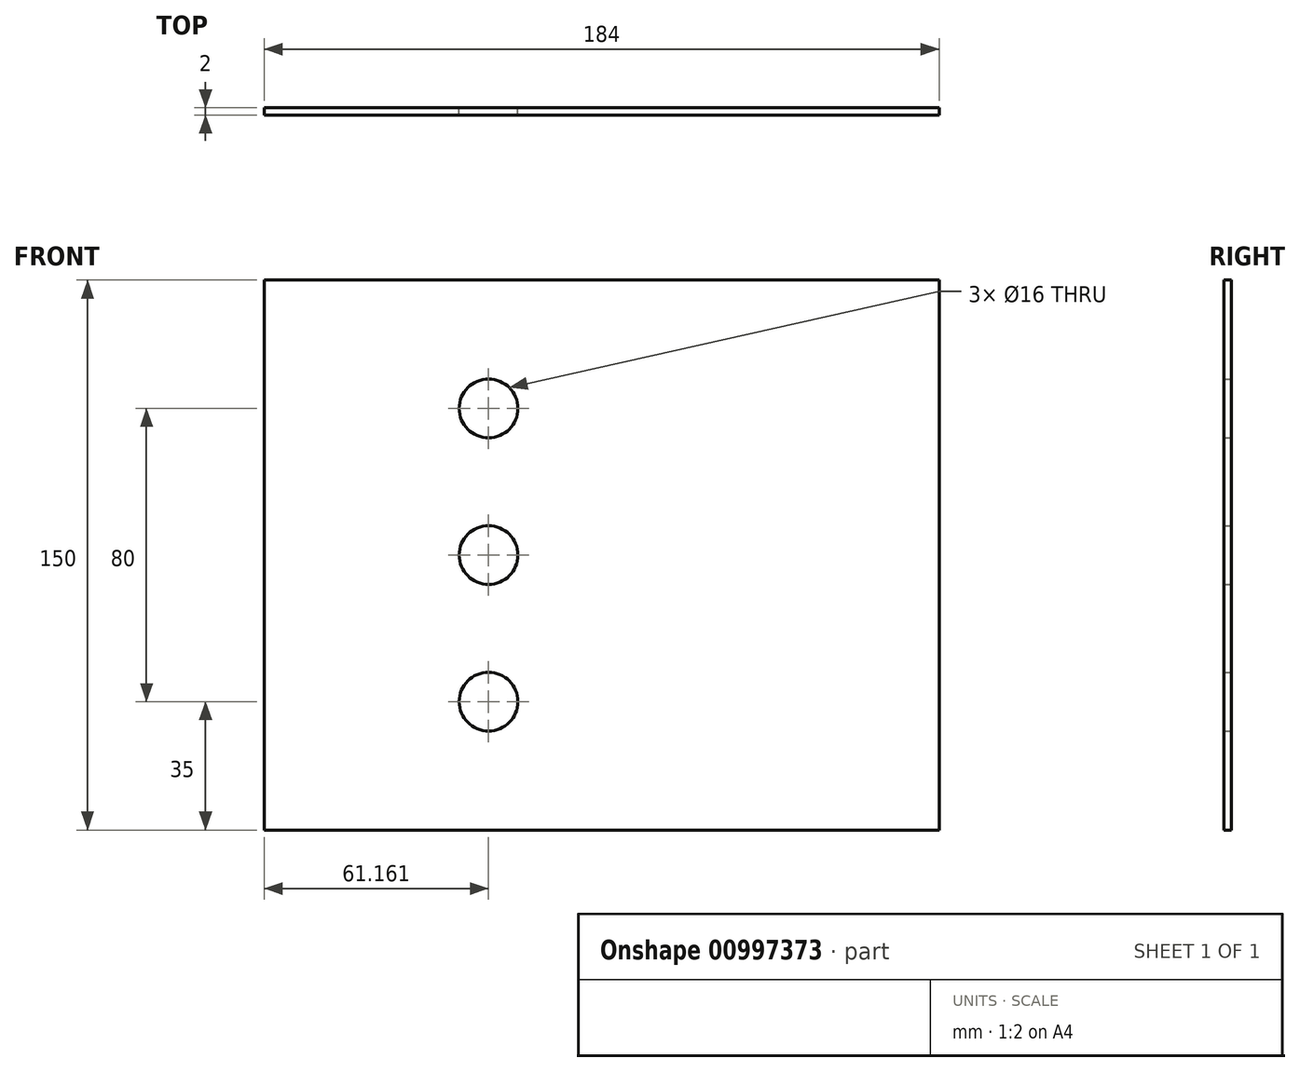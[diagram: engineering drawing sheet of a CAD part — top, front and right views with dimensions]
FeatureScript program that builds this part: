
annotation { "Feature Type Name" : "Feature", "Feature Type Description" : "" }
export const myFeature = defineFeature(function(context is Context, id is Id, definition is map)
    precondition{}
    {
        {
            var Q0;
            Q0=qCreatedBy(makeId("Front.planeOp"),FACE);
            var sketch = newSketch(context, id + "F0", { "sketchPlane" : qUnion([Q0])});
            skLineSegment(sketch, "E0.bottom", {"start": v(92, -75) * mm, "end": v(-92, -75) * mm});
            skLineSegment(sketch, "E0.top", {"start": v(92, 75) * mm, "end": v(-92, 75) * mm});
            skLineSegment(sketch, "E0.left", {"start": v(92, -75) * mm, "end": v(92, 75) * mm});
            skLineSegment(sketch, "E0.right", {"start": v(-92, -75) * mm, "end": v(-92, 75) * mm});
            skPoint(sketch, "E0.middle", {"position": v(0, 0) * mm});
            skCircle(sketch, "E1", {"center": v(-30.84, 40) * mm, "radius": 8 * mm});
            skCircle(sketch, "E2", {"center": v(-30.84, 0) * mm, "radius": 8 * mm});
            skCircle(sketch, "E3", {"center": v(-30.84, -40) * mm, "radius": 8 * mm});
            skSolve(sketch);
        }
        {
            var Q0;
            Q0=makeQuery(id+"F0.imprint","IMPRINT",FACE,{"disambiguationData":[TD([[makeQuery(id+"F0.imprint","IMPRINT",EDGE,{"derivedFrom":sQuery(id+"F0.wireOp",EDGE,"E0.bottom")}),-1.0]])]});
            extrude(context, id + "F1", {"entities" : qUnion([Q0]), "depth" : 2 * mm, "offsetDistance" : 25 * mm});
        }
    });
